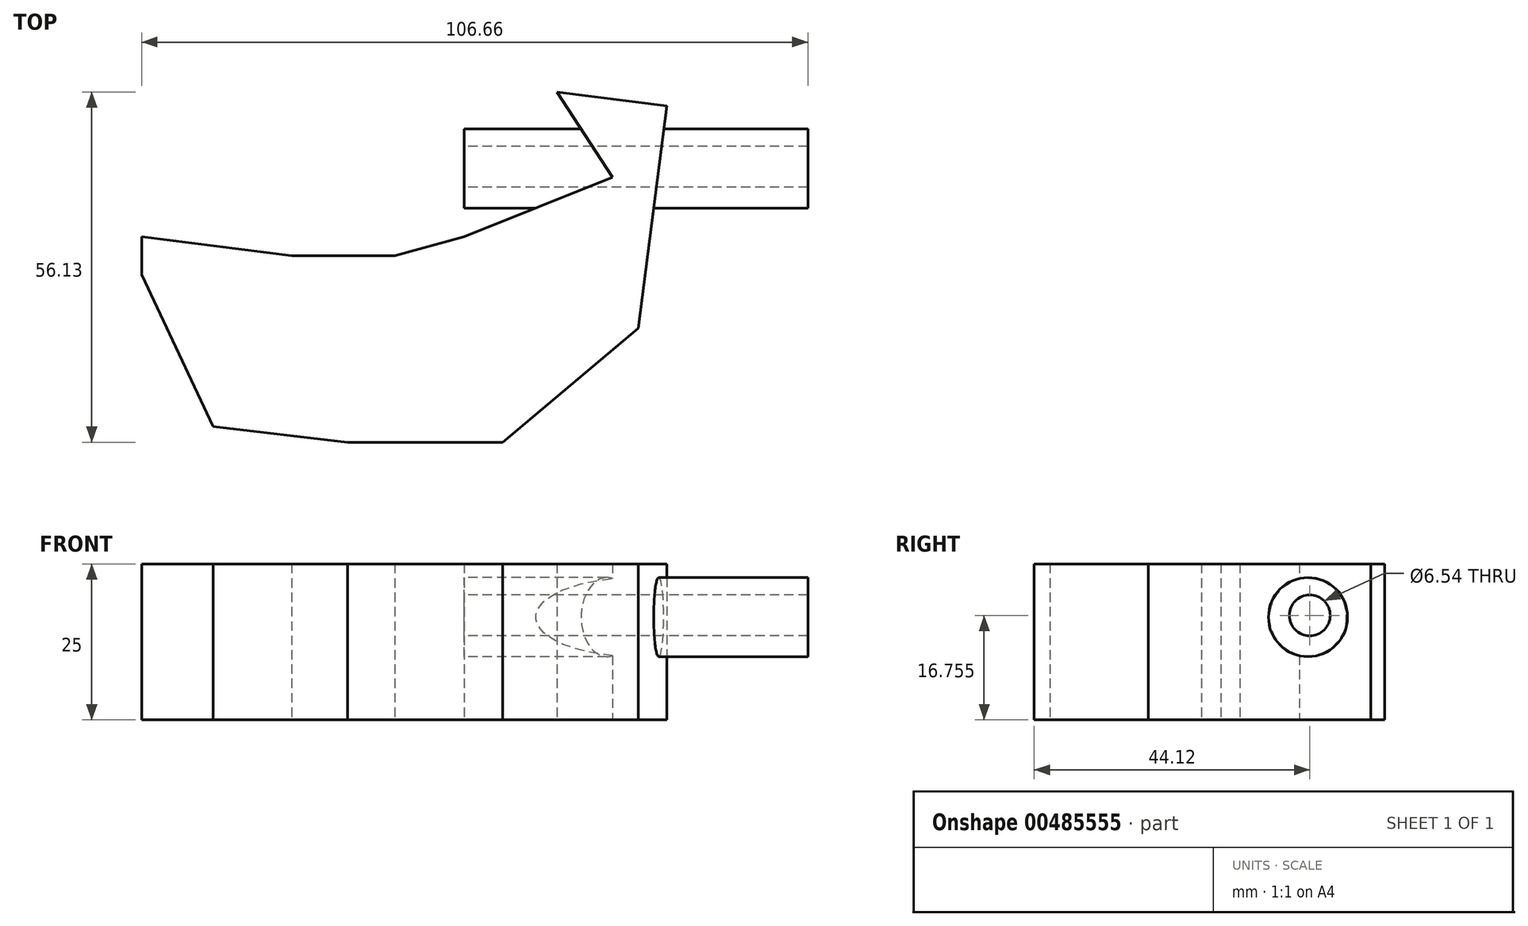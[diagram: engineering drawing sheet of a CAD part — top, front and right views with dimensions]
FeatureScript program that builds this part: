
annotation { "Feature Type Name" : "Feature", "Feature Type Description" : "" }
export const myFeature = defineFeature(function(context is Context, id is Id, definition is map)
    precondition{}
    {
        {
            var Q0;
            Q0=qCreatedBy(makeId("Top.planeOp"),FACE);
            var sketch = newSketch(context, id + "F0", { "sketchPlane" : qUnion([Q0])});
            skPoint(sketch, "E0.0", {"position": v(0, 0) * mm});
            skLineSegment(sketch, "E1", {"start": v(0, 0) * mm, "end": v(23.74, 9.5) * mm});
            skLineSegment(sketch, "E2", {"start": v(23.74, 9.5) * mm, "end": v(14.8, 23.18) * mm});
            skLineSegment(sketch, "E3", {"start": v(14.8, 23.18) * mm, "end": v(32.4, 20.94) * mm});
            skLineSegment(sketch, "E4", {"start": v(32.4, 20.94) * mm, "end": v(27.87, -14.66) * mm});
            skLineSegment(sketch, "E5", {"start": v(27.87, -14.66) * mm, "end": v(6.14, -32.95) * mm});
            skLineSegment(sketch, "E6", {"start": v(6.14, -32.95) * mm, "end": v(-18.71, -32.95) * mm});
            skLineSegment(sketch, "E7", {"start": v(-18.71, -32.95) * mm, "end": v(-40.21, -30.44) * mm});
            skLineSegment(sketch, "E8", {"start": v(-40.21, -30.44) * mm, "end": v(-51.66, -6.14) * mm});
            skLineSegment(sketch, "E9", {"start": v(-51.66, -6.14) * mm, "end": v(-51.66, 0) * mm});
            skLineSegment(sketch, "E10", {"start": v(-51.66, 0) * mm, "end": v(-27.65, -3.07) * mm});
            skLineSegment(sketch, "E11", {"start": v(-27.65, -3.07) * mm, "end": v(-11.17, -3.07) * mm});
            skLineSegment(sketch, "E12", {"start": v(-11.17, -3.07) * mm, "end": v(0, 0) * mm});
            skLineSegment(sketch, "E13", {"start": v(-20.94, -23.74) * mm, "end": v(-37.98, -39.65) * mm});
            skSolve(sketch);
        }
        {
            var Q0;
            Q0 = qSketchRegion(id + "F0", true);
            extrude(context, id + "F1", {"entities" : qUnion([Q0]), "depth" : 25 * mm});
        }
        {
            var Q0;
            Q0=qCreatedBy(makeId("Right.planeOp"),FACE);
            var sketch = newSketch(context, id + "F2", { "sketchPlane" : qUnion([Q0])});
            skCircle(sketch, "E14", {"center": v(10.9, 16.48) * mm, "radius": 6.33 * mm});
            skSolve(sketch);
        }
        {
            var Q0;
            Q0 = qSketchRegion(id + "F2", true);
            extrude(context, id + "F3", {"entities" : qUnion([Q0]), "operationType" : NewBodyOperationType.ADD, "depth" : 55 * mm});
        }
        {
            var Q0;
            Q0=qCreatedBy(makeId("Right.planeOp"),FACE);
            var sketch = newSketch(context, id + "F4", { "sketchPlane" : qUnion([Q0])});
            skCircle(sketch, "E15", {"center": v(10.9, 16.76) * mm, "radius": 4.55 * mm});
            skSolve(sketch);
        }
        {
            var Q0;
            Q0 = qSketchRegion(id + "F4", true);
            extrude(context, id + "F5", {"entities" : qUnion([Q0]), "operationType" : NewBodyOperationType.REMOVE, "endBound" : BoundingType.THROUGH_ALL, "oppositeDirection" : true, "depth" : 25 * mm});
        }
        {
            var Q0;
            Q0=qCreatedBy(makeId("Right.planeOp"),FACE);
            var sketch = newSketch(context, id + "F6", { "sketchPlane" : qUnion([Q0])});
            skCircle(sketch, "E16", {"center": v(11.17, 16.76) * mm, "radius": 3.27 * mm});
            skSolve(sketch);
        }
        {
            var Q0;
            Q0 = qSketchRegion(id + "F6", true);
            extrude(context, id + "F7", {"entities" : qUnion([Q0]), "operationType" : NewBodyOperationType.REMOVE, "endBound" : BoundingType.THROUGH_ALL, "depth" : 60 * mm});
        }
    });
